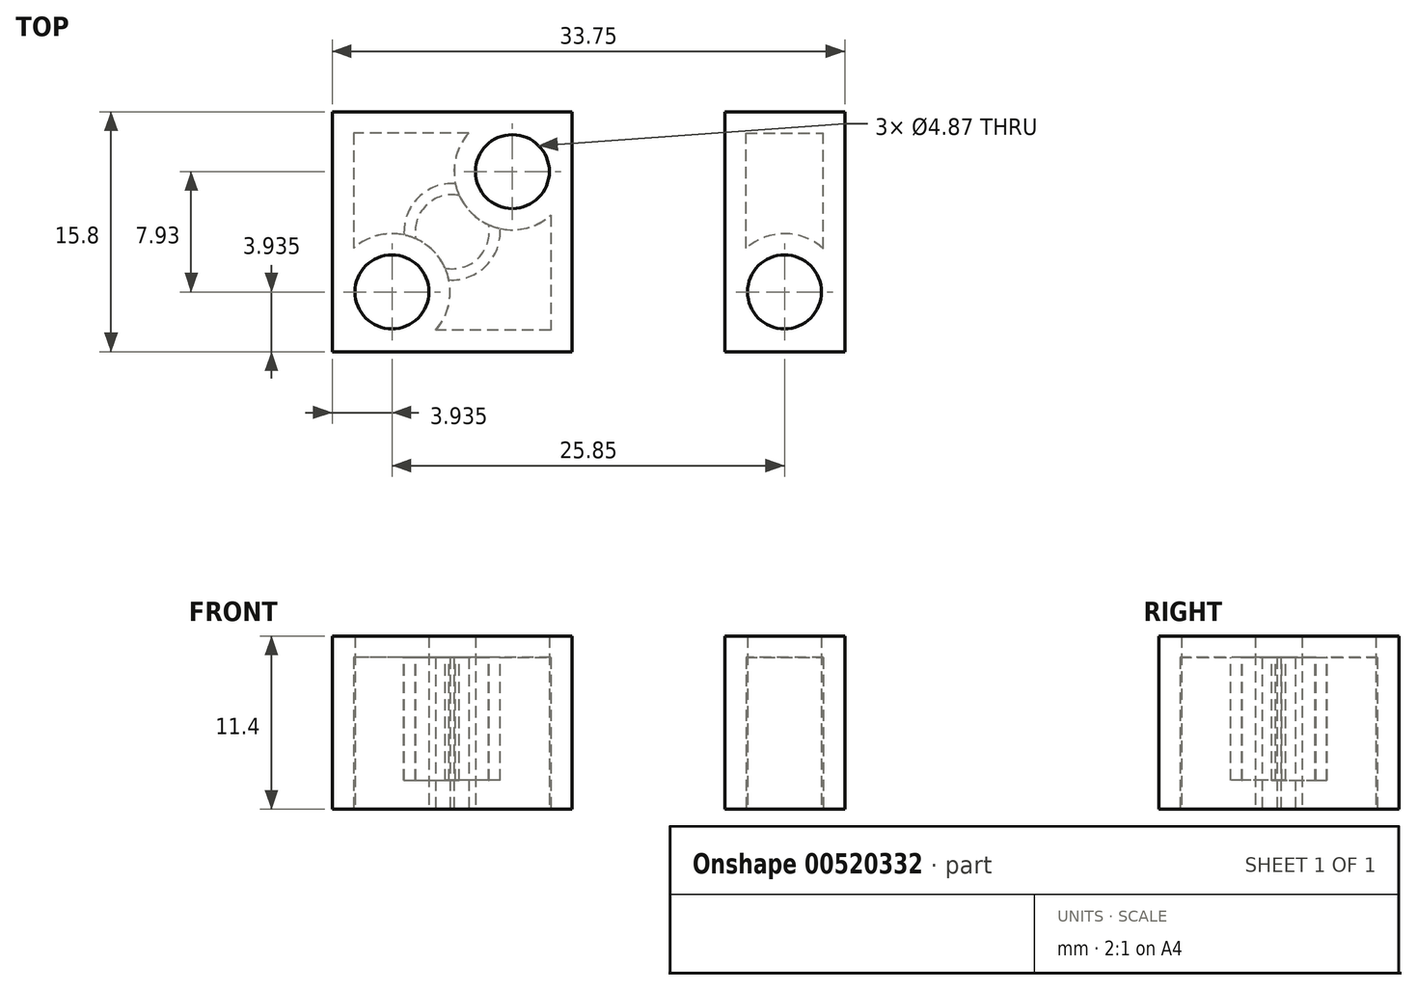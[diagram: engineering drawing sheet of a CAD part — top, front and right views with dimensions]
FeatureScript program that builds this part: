
annotation { "Feature Type Name" : "Feature", "Feature Type Description" : "" }
export const myFeature = defineFeature(function(context is Context, id is Id, definition is map)
    precondition{}
    {
        {
            var Q0;
            Q0=qCreatedBy(makeId("Top.planeOp"),FACE);
            var sketch = newSketch(context, id + "F0", { "sketchPlane" : qUnion([Q0])});
            skLineSegment(sketch, "E0.bottom", {"start": v(7.9, 7.9) * mm, "end": v(-7.9, 7.9) * mm});
            skLineSegment(sketch, "E0.top", {"start": v(7.9, -7.9) * mm, "end": v(-7.9, -7.9) * mm});
            skLineSegment(sketch, "E0.left", {"start": v(7.9, 7.9) * mm, "end": v(7.9, -7.9) * mm});
            skLineSegment(sketch, "E0.right", {"start": v(-7.9, 7.9) * mm, "end": v(-7.9, -7.9) * mm});
            skPoint(sketch, "E0.middle", {"position": v(0, 0) * mm});
            skPoint(sketch, "E1.orphan", {"position": v(-3.95, 0) * mm});
            skPoint(sketch, "E2.end.orphan", {"position": v(-7.9, 0) * mm});
            skPoint(sketch, "E3.end.orphan", {"position": v(7.9, 0) * mm});
            skPoint(sketch, "E4.end.orphan", {"position": v(0, 7.9) * mm});
            skPoint(sketch, "E5.end.orphan", {"position": v(0, -7.9) * mm});
            skLineSegment(sketch, "E6", {"start": v(0, 7.9) * mm, "end": v(0, 0) * mm});
            skPoint(sketch, "E7.start.orphan", {"position": v(0, 3.95) * mm});
            skLineSegment(sketch, "E8.bottom", {"start": v(17.95, -7.9) * mm, "end": v(25.85, -7.9) * mm});
            skLineSegment(sketch, "E8.top", {"start": v(17.95, 7.9) * mm, "end": v(25.85, 7.9) * mm});
            skLineSegment(sketch, "E8.left", {"start": v(17.95, -7.9) * mm, "end": v(17.95, 7.9) * mm});
            skLineSegment(sketch, "E8.right", {"start": v(25.85, -7.9) * mm, "end": v(25.85, 7.9) * mm});
            skLineSegment(sketch, "E9", {"start": v(17.95, 7.9) * mm, "end": v(17.95, 3.97) * mm});
            skLineSegment(sketch, "E10", {"start": v(17.95, 3.97) * mm, "end": v(21.88, 3.97) * mm});
            skCircle(sketch, "E11", {"center": v(21.88, 3.97) * mm, "radius": 2.44 * mm});
            skCircle(sketch, "E12.MirrorC", {"center": v(21.88, -3.97) * mm, "radius": 2.44 * mm});
            skPoint(sketch, "E13.start.orphan", {"position": v(-7.9, 3.95) * mm});
            skLineSegment(sketch, "E14", {"start": v(-7.9, 7.9) * mm, "end": v(-7.9, 3.96) * mm});
            skLineSegment(sketch, "E15", {"start": v(-7.9, 3.96) * mm, "end": v(-3.97, 3.96) * mm});
            skCircle(sketch, "E16", {"center": v(-3.97, 3.96) * mm, "radius": 2.44 * mm});
            skCircle(sketch, "E17.MirrorC", {"center": v(3.97, 3.96) * mm, "radius": 2.44 * mm});
            skCircle(sketch, "E18.MirrorC", {"center": v(3.97, -3.96) * mm, "radius": 2.44 * mm});
            skCircle(sketch, "E19.MirrorC", {"center": v(-3.97, -3.96) * mm, "radius": 2.44 * mm});
            skSolve(sketch);
        }
        {
            var Q0;
            Q0=makeQuery(id+"F0.imprint","IMPRINT",FACE,{"disambiguationData":[TD([[makeQuery(id+"F0.imprint","IMPRINT",EDGE,{"derivedFrom":sQuery(id+"F0.wireOp",EDGE,"E0.bottom")}),1.0]])]});
            extrude(context, id + "F1", {"entities" : qUnion([Q0]), "depth" : 9.6 * mm, "offsetDistance" : 25 * mm});
        }
        {
            var Q0;
            Q0=makeQuery(id+"F0.imprint","IMPRINT",FACE,{"disambiguationData":[TD([[makeQuery(id+"F0.imprint","IMPRINT",EDGE,{"derivedFrom":sQuery(id+"F0.wireOp",EDGE,"E16")}),1.0]])]});
            var Q1;
            Q1=makeQuery(id+"F0.imprint","IMPRINT",FACE,{"disambiguationData":[TD([[makeQuery(id+"F0.imprint","IMPRINT",EDGE,{"derivedFrom":sQuery(id+"F0.wireOp",EDGE,"E17.MirrorC")}),-1.0]])]});
            var Q2;
            Q2=makeQuery(id+"F0.imprint","IMPRINT",FACE,{"disambiguationData":[TD([[makeQuery(id+"F0.imprint","IMPRINT",EDGE,{"derivedFrom":sQuery(id+"F0.wireOp",EDGE,"E19.MirrorC")}),-1.0]])]});
            var Q3;
            Q3=makeQuery(id+"F0.imprint","IMPRINT",FACE,{"disambiguationData":[TD([[makeQuery(id+"F0.imprint","IMPRINT",EDGE,{"derivedFrom":sQuery(id+"F0.wireOp",EDGE,"E18.MirrorC")}),1.0]])]});
            extrude(context, id + "F2", {"entities" : qUnion([Q0, Q1, Q2, Q3]), "operationType" : NewBodyOperationType.ADD, "depth" : 11.4 * mm, "offsetDistance" : 25 * mm});
        }
        {
            var Q0;
            Q0=makeQuery(id+"F0.imprint","IMPRINT",FACE,{"disambiguationData":[TD([[makeQuery(id+"F0.imprint","IMPRINT",EDGE,{"derivedFrom":sQuery(id+"F0.wireOp",EDGE,"E8.bottom")}),1.0]])]});
            extrude(context, id + "F3", {"entities" : qUnion([Q0]), "depth" : 9.6 * mm, "offsetDistance" : 25 * mm});
        }
        {
            var Q0;
            Q0=makeQuery(id+"F0.imprint","IMPRINT",FACE,{"disambiguationData":[TD([[makeQuery(id+"F0.imprint","IMPRINT",EDGE,{"derivedFrom":sQuery(id+"F0.wireOp",EDGE,"E11")}),1.0]])]});
            var Q1;
            Q1=makeQuery(id+"F0.imprint","IMPRINT",FACE,{"disambiguationData":[TD([[makeQuery(id+"F0.imprint","IMPRINT",EDGE,{"derivedFrom":sQuery(id+"F0.wireOp",EDGE,"E12.MirrorC")}),-1.0]])]});
            extrude(context, id + "F4", {"entities" : qUnion([Q0, Q1]), "operationType" : NewBodyOperationType.ADD, "depth" : 11.4 * mm, "offsetDistance" : 25 * mm});
        }
        {
            var Q0;
            {var subQ0=sQuery(id+"F0.wireOp",EDGE,"E19.MirrorC");var subQ1=sQuery(id+"F0.wireOp",EDGE,"E18.MirrorC");var subQ2=sQuery(id+"F0.wireOp",EDGE,"E17.MirrorC");var subQ3=sQuery(id+"F0.wireOp",EDGE,"E16");Q0=makeQuery(id+"F2.boolean.opBoolean","MERGE",FACE,{"derivedFrom":[makeQuery(id+"F1.opExtrude","CAP_FACE",FACE,{"disambiguationData":[OSD([sQuery(id+"F0.wireOp",EDGE,"E0.bottom"),sQuery(id+"F0.wireOp",EDGE,"E0.top"),sQuery(id+"F0.wireOp",EDGE,"E0.left"),sQuery(id+"F0.wireOp",EDGE,"E0.right"),sQuery(id+"F0.wireOp",EDGE,"E14"),subQ3,subQ2,subQ1,subQ0])],"isStart":true}),makeQuery(id+"F2.opExtrude","CAP_FACE",FACE,{"disambiguationData":[OSD([subQ3])],"isStart":true}),makeQuery(id+"F2.opExtrude","CAP_FACE",FACE,{"disambiguationData":[OSD([subQ2])],"isStart":true}),makeQuery(id+"F2.opExtrude","CAP_FACE",FACE,{"disambiguationData":[OSD([subQ1])],"isStart":true}),makeQuery(id+"F2.opExtrude","CAP_FACE",FACE,{"disambiguationData":[OSD([subQ0])],"isStart":true})]});}
            var Q1;
            {var subQ0=sQuery(id+"F0.wireOp",EDGE,"E12.MirrorC");var subQ1=sQuery(id+"F0.wireOp",EDGE,"E11");Q1=makeQuery(id+"F4.boolean.opBoolean","MERGE",FACE,{"derivedFrom":[makeQuery(id+"F3.opExtrude","CAP_FACE",FACE,{"disambiguationData":[OSD([sQuery(id+"F0.wireOp",EDGE,"E8.bottom"),sQuery(id+"F0.wireOp",EDGE,"E8.top"),sQuery(id+"F0.wireOp",EDGE,"E8.left"),sQuery(id+"F0.wireOp",EDGE,"E8.right"),sQuery(id+"F0.wireOp",EDGE,"E9"),subQ1,subQ0])],"isStart":true}),makeQuery(id+"F4.opExtrude","CAP_FACE",FACE,{"disambiguationData":[OSD([subQ1])],"isStart":true}),makeQuery(id+"F4.opExtrude","CAP_FACE",FACE,{"disambiguationData":[OSD([subQ0])],"isStart":true})]});}
            shell(context, id + "F5", {"entities" : qUnion([Q0, Q1]), "thickness" : 1.4 * mm});
        }
        {
            var Q0;
            Q0=makeQuery(id+"F5.opShell","OFFSET_FACE",FACE,{"disambiguationData":[OSD([sQuery(id+"F0.wireOp",EDGE,"E0.bottom"),sQuery(id+"F0.wireOp",EDGE,"E0.top"),sQuery(id+"F0.wireOp",EDGE,"E0.left"),sQuery(id+"F0.wireOp",EDGE,"E0.right"),sQuery(id+"F0.wireOp",EDGE,"E14"),sQuery(id+"F0.wireOp",EDGE,"E16"),sQuery(id+"F0.wireOp",EDGE,"E17.MirrorC"),sQuery(id+"F0.wireOp",EDGE,"E18.MirrorC"),sQuery(id+"F0.wireOp",EDGE,"E19.MirrorC")])]});
            var sketch = newSketch(context, id + "F6", { "sketchPlane" : qUnion([Q0])});
            skCircle(sketch, "E20", {"center": v(0, 0) * mm, "radius": 3.17 * mm});
            skCircle(sketch, "E21", {"center": v(0, 0) * mm, "radius": 2.44 * mm});
            skSolve(sketch);
        }
        {
            var Q0;
            Q0 = qSketchRegion(id + "F6", true);
            extrude(context, id + "F7", {"entities" : qUnion([Q0]), "operationType" : NewBodyOperationType.ADD, "depth" : 8.1 * mm, "offsetDistance" : 25 * mm});
        }
    });
